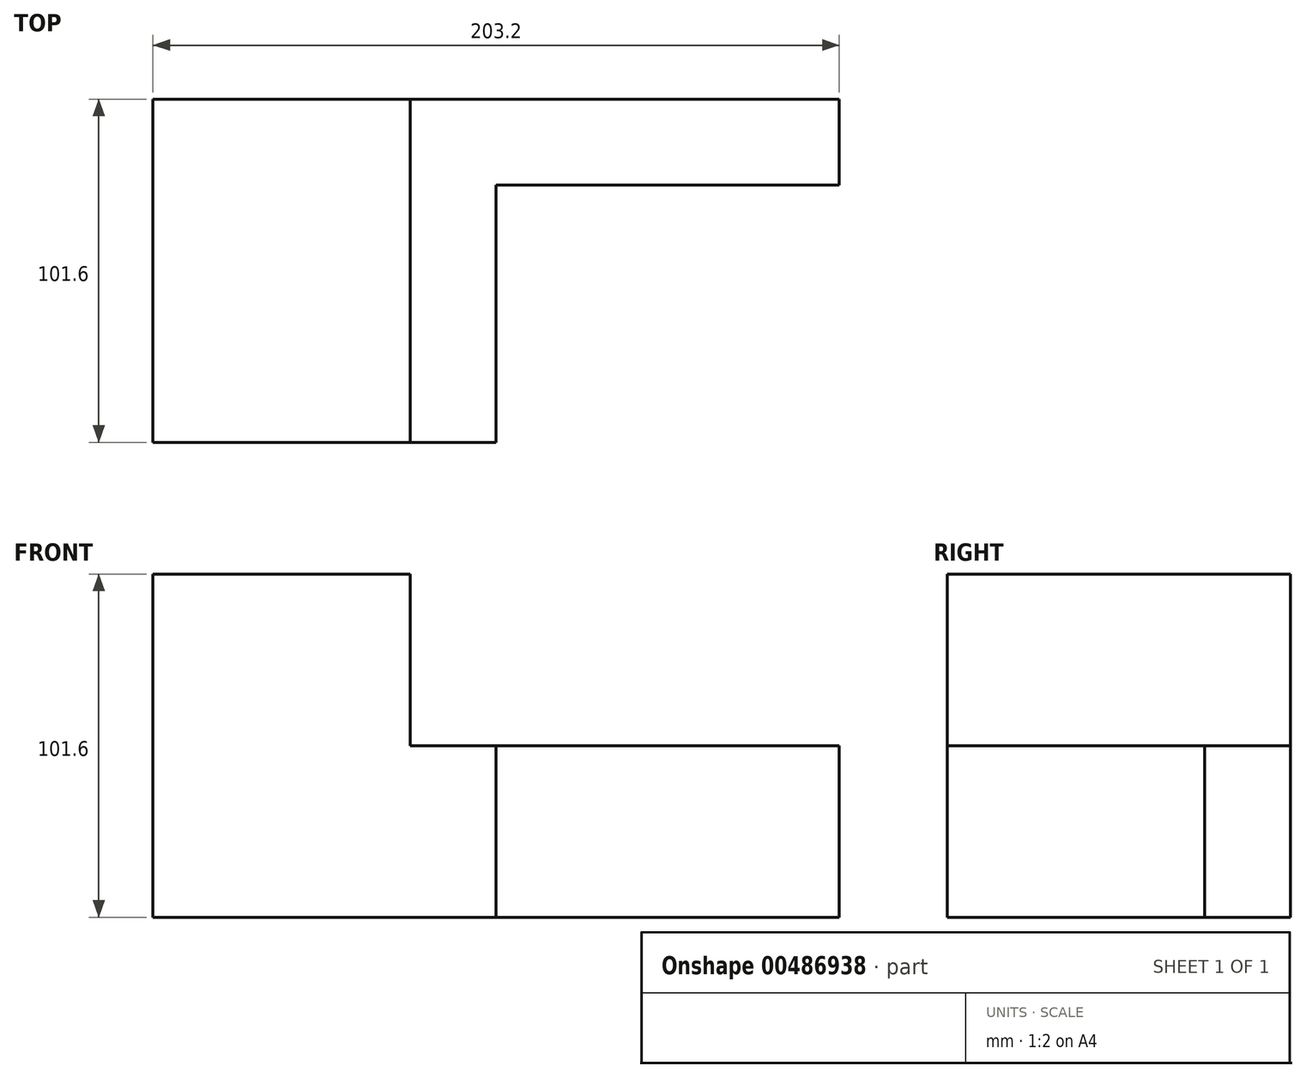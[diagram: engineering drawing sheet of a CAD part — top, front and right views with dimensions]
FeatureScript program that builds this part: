
annotation { "Feature Type Name" : "Feature", "Feature Type Description" : "" }
export const myFeature = defineFeature(function(context is Context, id is Id, definition is map)
    precondition{}
    {
        {
            var Q0;
            Q0=qCreatedBy(makeId("Front.planeOp"),FACE);
            var sketch = newSketch(context, id + "F0", { "sketchPlane" : qUnion([Q0])});
            skLineSegment(sketch, "E0.bottom", {"start": v(0, 0) * mm, "end": v(203.2, 0) * mm});
            skLineSegment(sketch, "E0.top", {"start": v(0, 101.6) * mm, "end": v(76.2, 101.6) * mm});
            skLineSegment(sketch, "E0.left", {"start": v(0, 0) * mm, "end": v(0, 101.6) * mm});
            skLineSegment(sketch, "E0.right", {"start": v(203.2, 0) * mm, "end": v(203.2, 50.8) * mm});
            skLineSegment(sketch, "E1", {"start": v(76.2, 101.6) * mm, "end": v(76.2, 50.8) * mm});
            skLineSegment(sketch, "E2", {"start": v(76.2, 50.8) * mm, "end": v(203.2, 50.8) * mm});
            skSolve(sketch);
        }
        {
            var Q0;
            Q0 = qSketchRegion(id + "F0", true);
            extrude(context, id + "F1", {"entities" : qUnion([Q0]), "depth" : 101.6 * mm});
        }
        {
            var Q0;
            Q0=makeQuery(id+"F1.opExtrude","SWEPT_FACE",FACE,{"disambiguationData":[OSD([sQuery(id+"F0.wireOp",EDGE,"E2")])]});
            var sketch = newSketch(context, id + "F2", { "sketchPlane" : qUnion([Q0])});
            skLineSegment(sketch, "E3.bottom", {"start": v(203.2, -101.6) * mm, "end": v(101.6, -101.6) * mm});
            skLineSegment(sketch, "E3.top", {"start": v(203.2, -25.4) * mm, "end": v(101.6, -25.4) * mm});
            skLineSegment(sketch, "E3.left", {"start": v(203.2, -101.6) * mm, "end": v(203.2, -25.4) * mm});
            skLineSegment(sketch, "E3.right", {"start": v(101.6, -101.6) * mm, "end": v(101.6, -25.4) * mm});
            skSolve(sketch);
        }
        {
            var Q0;
            Q0 = qSketchRegion(id + "F2", true);
            var Q1;
            {var subQ0=sQuery(id+"F2.wireOp",EDGE,"WZD6nUwi-S9EX-DX0k-dt9w-ggrFZSsODyII.bottom");Q1=makeQuery(id+"F2.imprint","IMPRINT",FACE,{"disambiguationData":[TD([[makeQuery(id+"F2.imprint","IMPRINT",EDGE,{"derivedFrom":subQ0}),1.0]])]});}
            extrude(context, id + "F3", {"entities" : qUnion([Q0, Q1]), "operationType" : NewBodyOperationType.REMOVE, "oppositeDirection" : true, "depth" : 50.8 * mm});
        }
        {
            var Q0;
            Q0 = qSketchRegion(id + "F2", true);
            extrude(context, id + "F4", {"entities" : qUnion([Q0]), "operationType" : NewBodyOperationType.REMOVE, "oppositeDirection" : true, "depth" : 50.8 * mm});
        }
    });
